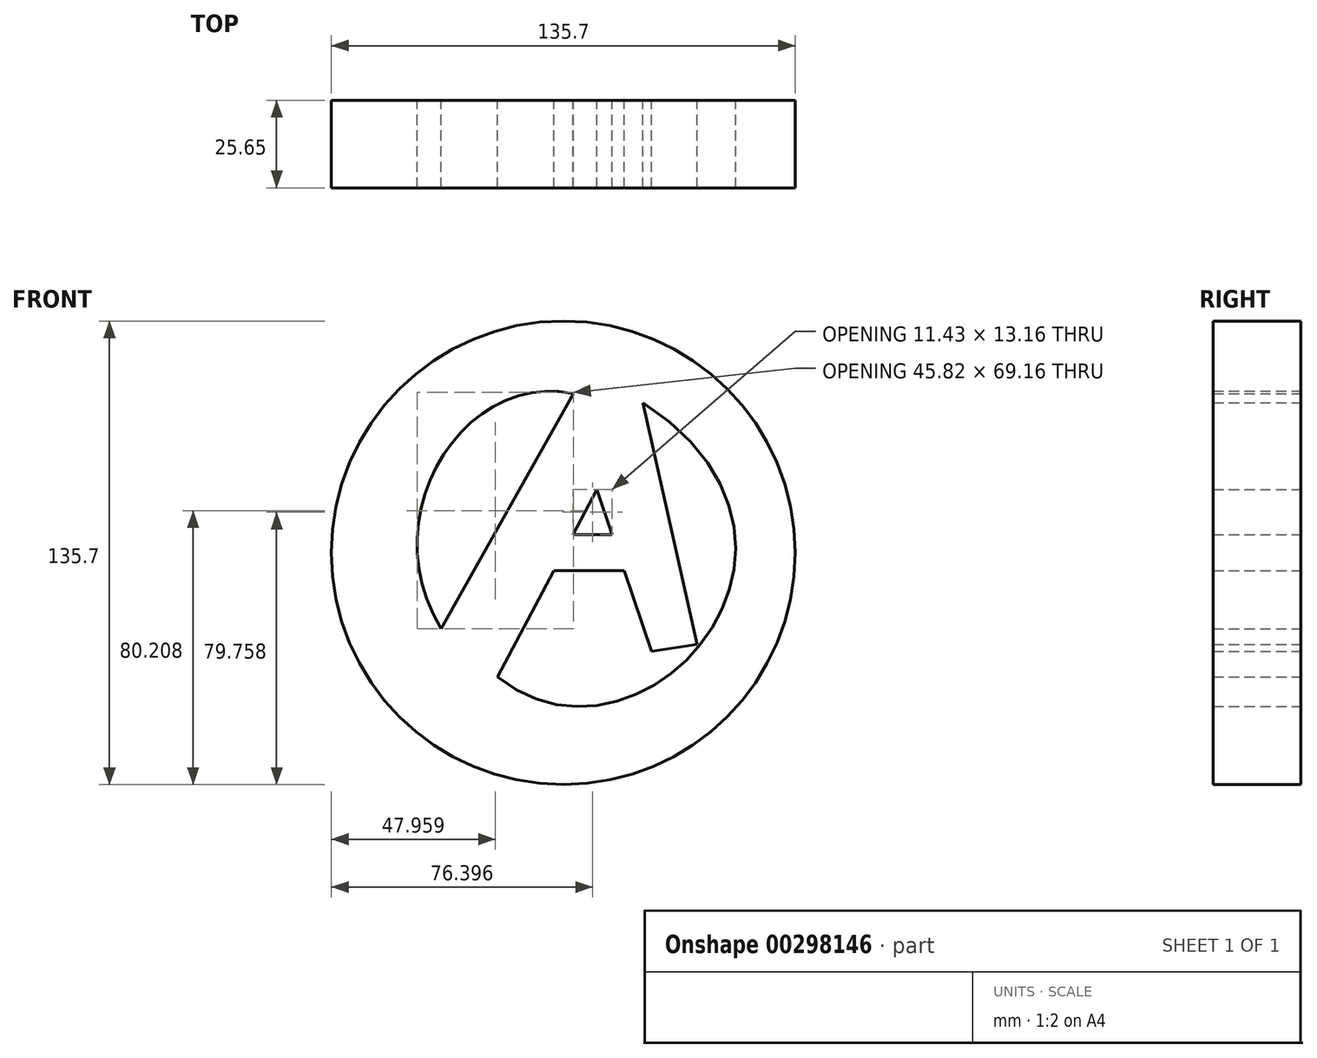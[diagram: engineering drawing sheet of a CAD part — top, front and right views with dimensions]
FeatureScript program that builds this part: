
annotation { "Feature Type Name" : "Feature", "Feature Type Description" : "" }
export const myFeature = defineFeature(function(context is Context, id is Id, definition is map)
    precondition{}
    {
        {
            var Q0;
            Q0=qCreatedBy(makeId("Front.planeOp"),FACE);
            var sketch = newSketch(context, id + "F0", { "sketchPlane" : qUnion([Q0])});
            skArc(sketch, "E0", {"start": v(-45.02, 18.05) * mm, "mid": v(-44.99, 17.98) * mm, "end": v(-44.93, 17.93) * mm});
            skLineSegment(sketch, "E1", {"start": v(-37.03, -46.29) * mm, "end": v(13.66, 43.75) * mm});
            skLineSegment(sketch, "E2", {"start": v(13.66, 43.75) * mm, "end": v(29.72, 33.5) * mm});
            skLineSegment(sketch, "E3", {"start": v(29.72, 33.5) * mm, "end": v(-17.9, -56.14) * mm});
            skLineSegment(sketch, "E4", {"start": v(-17.9, -56.14) * mm, "end": v(-35.55, -48.97) * mm});
            skLineSegment(sketch, "E5", {"start": v(29.72, 33.5) * mm, "end": v(45.57, -37.22) * mm});
            skLineSegment(sketch, "E6", {"start": v(45.57, -37.22) * mm, "end": v(32.17, -39.23) * mm});
            skLineSegment(sketch, "E7", {"start": v(32.17, -39.23) * mm, "end": v(16.21, 8.08) * mm});
            skFitSpline(sketch, "E8", {"points": [v(-29.34, -32.63) * mm, v(9.4, 36.2) * mm], "startDerivative": vector(-60.75, 97.9) * mm, "endDerivative": vector(97.65, -20.34) * mm});
            skFitSpline(sketch, "E9", {"points": [v(29.72, 33.5) * mm, v(-12.9, -46.73) * mm], "startDerivative": vector(192.53, -124.33) * mm, "endDerivative": vector(-126.72, 101.27) * mm});
            skCircle(sketch, "E10", {"center": v(6.4, -10.4) * mm, "radius": 67.85 * mm});
            skLineSegment(sketch, "E11", {"start": v(9.22, -5.08) * mm, "end": v(20.65, -5.08) * mm});
            skLineSegment(sketch, "E12", {"start": v(20.65, -5.08) * mm, "end": v(24.19, -15.58) * mm});
            skLineSegment(sketch, "E13", {"start": v(24.19, -15.58) * mm, "end": v(3.65, -15.58) * mm});
            skLineSegment(sketch, "E14.left", {"start": v(20.65, 0) * mm, "end": v(20.65, -1.85) * mm});
            skLineSegment(sketch, "E14.right", {"start": v(37.65, 0) * mm, "end": v(37.65, -1.85) * mm});
            skSolve(sketch);
        }
        {
            var Q0;
            {var subQ4=sQuery(id+"F0.wireOp",EDGE,"E8");Q0=makeQuery(id+"F0.imprint","IMPRINT",FACE,{"disambiguationData":[TD([[makeQuery(id+"F0.imprint","IMPRINT",EDGE,{"derivedFrom":subQ4}),1.0]])]});}
            extrude(context, id + "F1", {"entities" : qUnion([Q0]), "endBound" : BoundingType.SYMMETRIC, "depth" : 25.4 * mm});
        }
        {
            var Q0;
            {var subQ1=sQuery(id+"F0.wireOp",EDGE,"E5");Q0=makeQuery(id+"F0.imprint","IMPRINT",FACE,{"disambiguationData":[TD([[makeQuery(id+"F0.imprint","IMPRINT",EDGE,{"derivedFrom":subQ1}),-1.0]])]});}
            extrude(context, id + "F2", {"entities" : qUnion([Q0]), "operationType" : NewBodyOperationType.ADD, "endBound" : BoundingType.SYMMETRIC, "depth" : 25.4 * mm});
        }
        {
            var Q0;
            {var subQ0=sQuery(id+"F0.wireOp",EDGE,"E11");Q0=makeQuery(id+"F0.imprint","IMPRINT",FACE,{"disambiguationData":[TD([[makeQuery(id+"F0.imprint","IMPRINT",EDGE,{"derivedFrom":subQ0}),-1.0]])]});}
            extrude(context, id + "F3", {"entities" : qUnion([Q0]), "operationType" : NewBodyOperationType.ADD, "endBound" : BoundingType.SYMMETRIC, "depth" : 25.4 * mm});
        }
        {
            var Q0;
            Q0=makeQuery(id+"F2.opExtrude","CAP_FACE",FACE,{"disambiguationData":[OSD([sQuery(id+"F0.wireOp",EDGE,"E5"),sQuery(id+"F0.wireOp",EDGE,"E6"),sQuery(id+"F0.wireOp",EDGE,"E7"),sQuery(id+"F0.wireOp",EDGE,"ufSd37YV-pg3L-p8PC-eDYt-ASXeSWQUCoT3")])],"isStart":false});
            extrude(context, id + "F4", {"entities" : qUnion([Q0]), "operationType" : NewBodyOperationType.ADD, "endBound" : BoundingType.SYMMETRIC, "oppositeDirection" : true, "depth" : 0.5 * mm});
        }
    });
